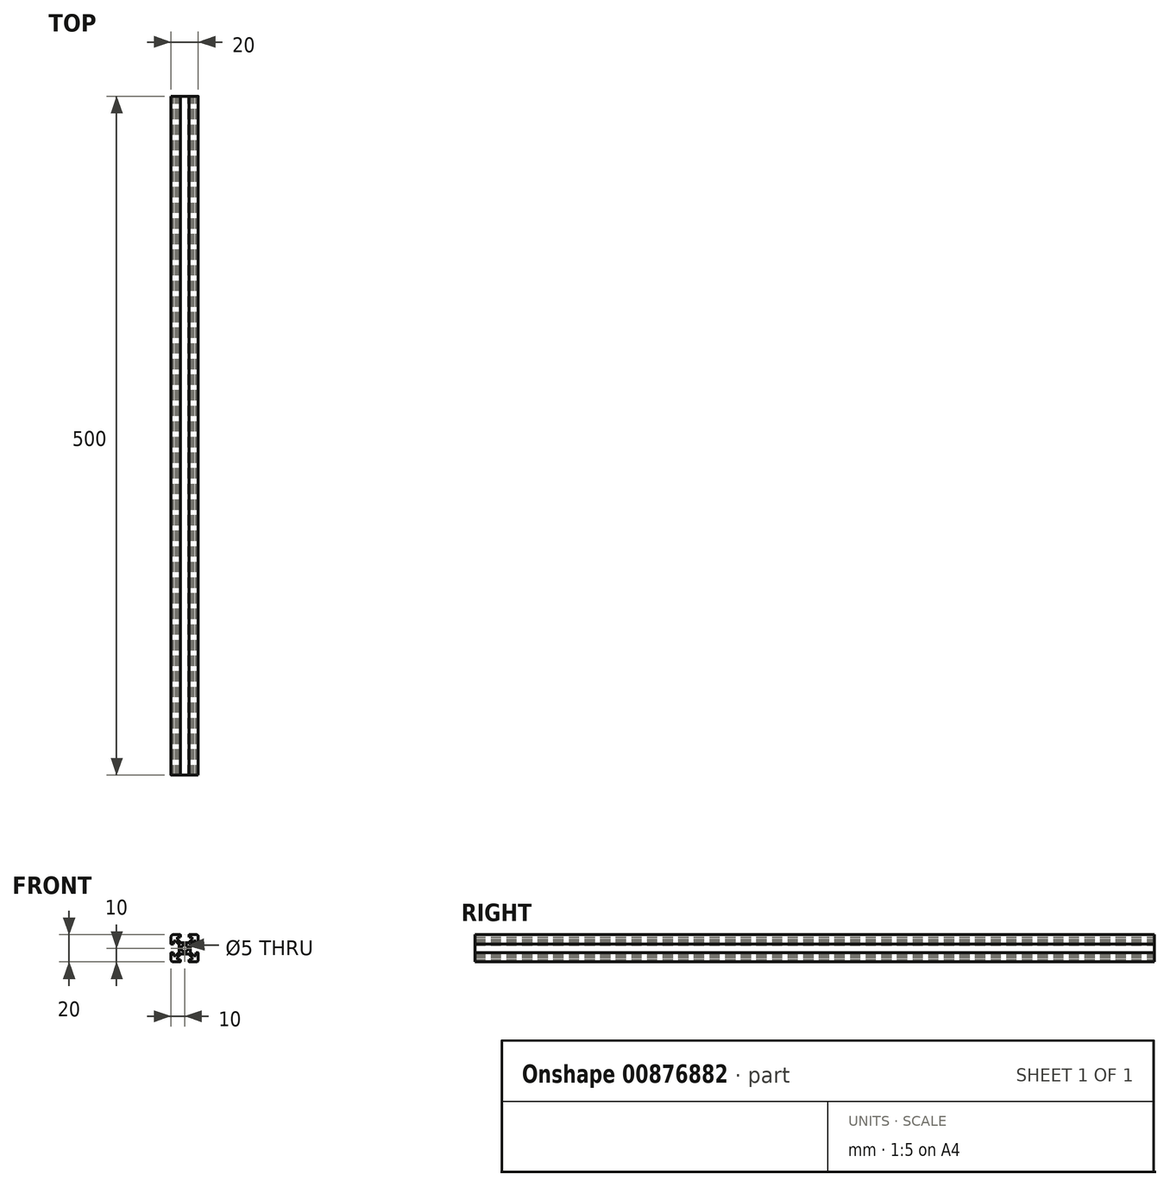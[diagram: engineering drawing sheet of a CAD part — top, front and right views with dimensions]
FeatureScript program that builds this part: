
annotation { "Feature Type Name" : "Feature", "Feature Type Description" : "" }
export const myFeature = defineFeature(function(context is Context, id is Id, definition is map)
    precondition{}
    {
        {
            var Q0;
            Q0=qCreatedBy(makeId("Front.planeOp"),FACE);
            var sketch = newSketch(context, id + "F0", { "sketchPlane" : qUnion([Q0])});
            skLineSegment(sketch, "E0.bottom", {"start": v(-10, 10) * mm, "end": v(10, 10) * mm});
            skLineSegment(sketch, "E0.top", {"start": v(-10, -10) * mm, "end": v(10, -10) * mm});
            skLineSegment(sketch, "E0.left", {"start": v(-10, 10) * mm, "end": v(-10, -10) * mm});
            skLineSegment(sketch, "E0.right", {"start": v(10, 10) * mm, "end": v(10, -10) * mm});
            skPoint(sketch, "E0.middle", {"position": v(0, 0) * mm});
            skLineSegment(sketch, "E1", {"start": v(8.2, 3.1) * mm, "end": v(10, 3.1) * mm});
            skLineSegment(sketch, "E2.MirrorCS", {"start": v(8.2, -3.1) * mm, "end": v(10, -3.1) * mm});
            skLineSegment(sketch, "E3", {"start": v(8.2, 3.1) * mm, "end": v(8.2, 5.5) * mm});
            skLineSegment(sketch, "E4.MirrorCS", {"start": v(8.2, -3.1) * mm, "end": v(8.2, -5.5) * mm});
            skLineSegment(sketch, "E5", {"start": v(8.2, 5.5) * mm, "end": v(6.6, 5.5) * mm});
            skLineSegment(sketch, "E6.MirrorCS", {"start": v(8.2, -5.5) * mm, "end": v(6.6, -5.5) * mm});
            skCircle(sketch, "E7", {"center": v(0, 0) * mm, "radius": 2.5 * mm});
            skLineSegment(sketch, "E8", {"start": v(4.1, 3) * mm, "end": v(4.1, -3) * mm});
            skLineSegment(sketch, "E9", {"start": v(4.1, 3) * mm, "end": v(6.6, 5.5) * mm});
            skLineSegment(sketch, "E10.MirrorCS", {"start": v(4.1, -3) * mm, "end": v(6.6, -5.5) * mm});
            skLineSegment(sketch, "E11.MirrorCS", {"start": v(-8.2, 3.1) * mm, "end": v(-10, 3.1) * mm});
            skLineSegment(sketch, "E12.MirrorCS", {"start": v(-8.2, 3.1) * mm, "end": v(-8.2, 5.5) * mm});
            skLineSegment(sketch, "E13.MirrorCS", {"start": v(-8.2, 5.5) * mm, "end": v(-6.6, 5.5) * mm});
            skLineSegment(sketch, "E14.MirrorCS", {"start": v(-4.1, 3) * mm, "end": v(-6.6, 5.5) * mm});
            skLineSegment(sketch, "E15.MirrorCS", {"start": v(-4.1, 3) * mm, "end": v(-4.1, -3) * mm});
            skLineSegment(sketch, "E16.MirrorCS", {"start": v(-4.1, -3) * mm, "end": v(-6.6, -5.5) * mm});
            skLineSegment(sketch, "E17.MirrorCS", {"start": v(-8.2, -5.5) * mm, "end": v(-6.6, -5.5) * mm});
            skLineSegment(sketch, "E18.MirrorCS", {"start": v(-8.2, -3.1) * mm, "end": v(-8.2, -5.5) * mm});
            skLineSegment(sketch, "E19.MirrorCS", {"start": v(-8.2, -3.1) * mm, "end": v(-10, -3.1) * mm});
            skLineSegment(sketch, "E20", {"start": v(-3.1, 10) * mm, "end": v(-3.1, 8.2) * mm});
            skLineSegment(sketch, "E21", {"start": v(-3.1, 8.2) * mm, "end": v(-5.5, 8.2) * mm});
            skLineSegment(sketch, "E22", {"start": v(-5.5, 8.2) * mm, "end": v(-5.5, 6.6) * mm});
            skLineSegment(sketch, "E23", {"start": v(-3, 4.1) * mm, "end": v(0, 4.1) * mm});
            skLineSegment(sketch, "E24.MirrorCS", {"start": v(3.1, 10) * mm, "end": v(3.1, 8.2) * mm});
            skLineSegment(sketch, "E25.MirrorCS", {"start": v(3.1, 8.2) * mm, "end": v(5.5, 8.2) * mm});
            skLineSegment(sketch, "E26.MirrorCS", {"start": v(5.5, 8.2) * mm, "end": v(5.5, 6.6) * mm});
            skLineSegment(sketch, "E27.MirrorCS", {"start": v(3, 4.1) * mm, "end": v(0, 4.1) * mm});
            skLineSegment(sketch, "E28", {"start": v(5.5, 6.6) * mm, "end": v(3, 4.1) * mm});
            skLineSegment(sketch, "E29", {"start": v(-5.5, 6.6) * mm, "end": v(-3, 4.1) * mm});
            skLineSegment(sketch, "E30.MirrorCS", {"start": v(-3.1, -10) * mm, "end": v(-3.1, -8.2) * mm});
            skLineSegment(sketch, "E31.MirrorCS", {"start": v(-3.1, -8.2) * mm, "end": v(-5.5, -8.2) * mm});
            skLineSegment(sketch, "E32.MirrorCS", {"start": v(-5.5, -8.2) * mm, "end": v(-5.5, -6.6) * mm});
            skLineSegment(sketch, "E33.MirrorCS", {"start": v(-5.5, -6.6) * mm, "end": v(-3, -4.1) * mm});
            skLineSegment(sketch, "E34.MirrorCS", {"start": v(3.1, -10) * mm, "end": v(3.1, -8.2) * mm});
            skLineSegment(sketch, "E35.MirrorCS", {"start": v(3.1, -8.2) * mm, "end": v(5.5, -8.2) * mm});
            skLineSegment(sketch, "E36.MirrorCS", {"start": v(5.5, -8.2) * mm, "end": v(5.5, -6.6) * mm});
            skLineSegment(sketch, "E37.MirrorCS", {"start": v(5.5, -6.6) * mm, "end": v(3, -4.1) * mm});
            skLineSegment(sketch, "E38.MirrorCS", {"start": v(3, -4.1) * mm, "end": v(0, -4.1) * mm});
            skLineSegment(sketch, "E39.MirrorCS", {"start": v(-3, -4.1) * mm, "end": v(0, -4.1) * mm});
            skSolve(sketch);
        }
        {
            var Q0;
            {var subQ5=sQuery(id+"F0.wireOp",EDGE,"E1");Q0=makeQuery(id+"F0.imprint","IMPRINT",FACE,{"disambiguationData":[TD([[makeQuery(id+"F0.imprint","IMPRINT",EDGE,{"derivedFrom":subQ5}),1.0]])]});}
            var Q1;
            {var subQ5=sQuery(id+"F0.wireOp",EDGE,"cca19c45-e8a9-4585-a149-2eca36f272d1");Q1=makeQuery(id+"F0.imprint","IMPRINT",FACE,{"disambiguationData":[TD([[makeQuery(id+"F0.imprint","IMPRINT",EDGE,{"derivedFrom":subQ5}),1.0]])]});}
            var Q2;
            {var subQ5=sQuery(id+"F0.wireOp",EDGE,"d64c8d37-8164-4fb8-9df1-a9879065921b");Q2=makeQuery(id+"F0.imprint","IMPRINT",FACE,{"disambiguationData":[TD([[makeQuery(id+"F0.imprint","IMPRINT",EDGE,{"derivedFrom":subQ5}),1.0]])]});}
            extrude(context, id + "F1", {"entities" : qUnion([Q0, Q1, Q2]), "depth" : 500 * mm, "offsetDistance" : 25 * mm});
        }
        {
            var Q0;
            Q0=makeQuery(id+"F1.opExtrude","SWEPT_EDGE",EDGE,{"disambiguationData":[OSD([sQuery(id+"F0.wireOp",EDGE,"E0.bottom"),sQuery(id+"F0.wireOp",EDGE,"E0.left")])]});
            var Q1;
            Q1=makeQuery(id+"F1.opExtrude","SWEPT_EDGE",EDGE,{"disambiguationData":[OSD([sQuery(id+"F0.wireOp",EDGE,"E0.bottom"),sQuery(id+"F0.wireOp",EDGE,"E0.right")])]});
            var Q2;
            Q2=makeQuery(id+"F1.opExtrude","SWEPT_EDGE",EDGE,{"disambiguationData":[OSD([sQuery(id+"F0.wireOp",EDGE,"E0.top"),sQuery(id+"F0.wireOp",EDGE,"E0.right")])]});
            var Q3;
            Q3=makeQuery(id+"F1.opExtrude","SWEPT_EDGE",EDGE,{"disambiguationData":[OSD([sQuery(id+"F0.wireOp",EDGE,"E0.top"),sQuery(id+"F0.wireOp",EDGE,"E0.left")])]});
            fillet(context, id + "F2", {"entities" : qUnion([Q0, Q1, Q2, Q3]), "radius" : 1.5 * mm, "tangentPropagation" : true, "allowEdgeOverflow" : false});
        }
        {
            var Q0;
            Q0=makeQuery(id+"F1.opExtrude","SWEPT_EDGE",EDGE,{"disambiguationData":[OSD([sQuery(id+"F0.wireOp",EDGE,"E14.MirrorCS"),sQuery(id+"F0.wireOp",EDGE,"E15.MirrorCS")])]});
            var Q1;
            Q1=makeQuery(id+"F1.opExtrude","SWEPT_EDGE",EDGE,{"disambiguationData":[OSD([sQuery(id+"F0.wireOp",EDGE,"E15.MirrorCS"),sQuery(id+"F0.wireOp",EDGE,"E16.MirrorCS")])]});
            var Q2;
            Q2=makeQuery(id+"F1.opExtrude","SWEPT_EDGE",EDGE,{"disambiguationData":[OSD([sQuery(id+"F0.wireOp",EDGE,"E27.MirrorCS"),sQuery(id+"F0.wireOp",EDGE,"E28")])]});
            var Q3;
            Q3=makeQuery(id+"F1.opExtrude","SWEPT_EDGE",EDGE,{"disambiguationData":[OSD([sQuery(id+"F0.wireOp",EDGE,"E23"),sQuery(id+"F0.wireOp",EDGE,"E29")])]});
            var Q4;
            Q4=makeQuery(id+"F1.opExtrude","SWEPT_EDGE",EDGE,{"disambiguationData":[OSD([sQuery(id+"F0.wireOp",EDGE,"E8"),sQuery(id+"F0.wireOp",EDGE,"E9")])]});
            var Q5;
            Q5=makeQuery(id+"F1.opExtrude","SWEPT_EDGE",EDGE,{"disambiguationData":[OSD([sQuery(id+"F0.wireOp",EDGE,"E8"),sQuery(id+"F0.wireOp",EDGE,"E10.MirrorCS")])]});
            var Q6;
            Q6=makeQuery(id+"F1.opExtrude","SWEPT_EDGE",EDGE,{"disambiguationData":[OSD([sQuery(id+"F0.wireOp",EDGE,"E37.MirrorCS"),sQuery(id+"F0.wireOp",EDGE,"E38.MirrorCS")])]});
            var Q7;
            Q7=makeQuery(id+"F1.opExtrude","SWEPT_EDGE",EDGE,{"disambiguationData":[OSD([sQuery(id+"F0.wireOp",EDGE,"E33.MirrorCS"),sQuery(id+"F0.wireOp",EDGE,"E39.MirrorCS")])]});
            fillet(context, id + "F3", {"entities" : qUnion([Q0, Q1, Q2, Q3, Q4, Q5, Q6, Q7]), "radius" : 2 * mm, "tangentPropagation" : true, "allowEdgeOverflow" : false});
        }
        {
            var Q0;
            Q0=makeQuery(id+"F1.opExtrude","SWEPT_EDGE",EDGE,{"disambiguationData":[OSD([sQuery(id+"F0.wireOp",EDGE,"E0.left"),sQuery(id+"F0.wireOp",EDGE,"E11.MirrorCS")])]});
            var Q1;
            Q1=makeQuery(id+"F1.opExtrude","SWEPT_EDGE",EDGE,{"disambiguationData":[OSD([sQuery(id+"F0.wireOp",EDGE,"E0.top"),sQuery(id+"F0.wireOp",EDGE,"E30.MirrorCS")])]});
            var Q2;
            Q2=makeQuery(id+"F1.opExtrude","SWEPT_EDGE",EDGE,{"disambiguationData":[OSD([sQuery(id+"F0.wireOp",EDGE,"E0.top"),sQuery(id+"F0.wireOp",EDGE,"E34.MirrorCS")])]});
            var Q3;
            Q3=makeQuery(id+"F1.opExtrude","SWEPT_EDGE",EDGE,{"disambiguationData":[OSD([sQuery(id+"F0.wireOp",EDGE,"E0.right"),sQuery(id+"F0.wireOp",EDGE,"E2.MirrorCS")])]});
            var Q4;
            Q4=makeQuery(id+"F1.opExtrude","SWEPT_EDGE",EDGE,{"disambiguationData":[OSD([sQuery(id+"F0.wireOp",EDGE,"E0.right"),sQuery(id+"F0.wireOp",EDGE,"E1")])]});
            var Q5;
            Q5=makeQuery(id+"F1.opExtrude","SWEPT_EDGE",EDGE,{"disambiguationData":[OSD([sQuery(id+"F0.wireOp",EDGE,"E0.left"),sQuery(id+"F0.wireOp",EDGE,"E19.MirrorCS")])]});
            var Q6;
            Q6=makeQuery(id+"F1.opExtrude","SWEPT_EDGE",EDGE,{"disambiguationData":[OSD([sQuery(id+"F0.wireOp",EDGE,"E0.bottom"),sQuery(id+"F0.wireOp",EDGE,"E24.MirrorCS")])]});
            var Q7;
            Q7=makeQuery(id+"F1.opExtrude","SWEPT_EDGE",EDGE,{"disambiguationData":[OSD([sQuery(id+"F0.wireOp",EDGE,"E0.bottom"),sQuery(id+"F0.wireOp",EDGE,"E20")])]});
            fillet(context, id + "F4", {"entities" : qUnion([Q0, Q1, Q2, Q3, Q4, Q5, Q6, Q7]), "radius" : 0.2 * mm, "tangentPropagation" : true, "allowEdgeOverflow" : false});
        }
    });
